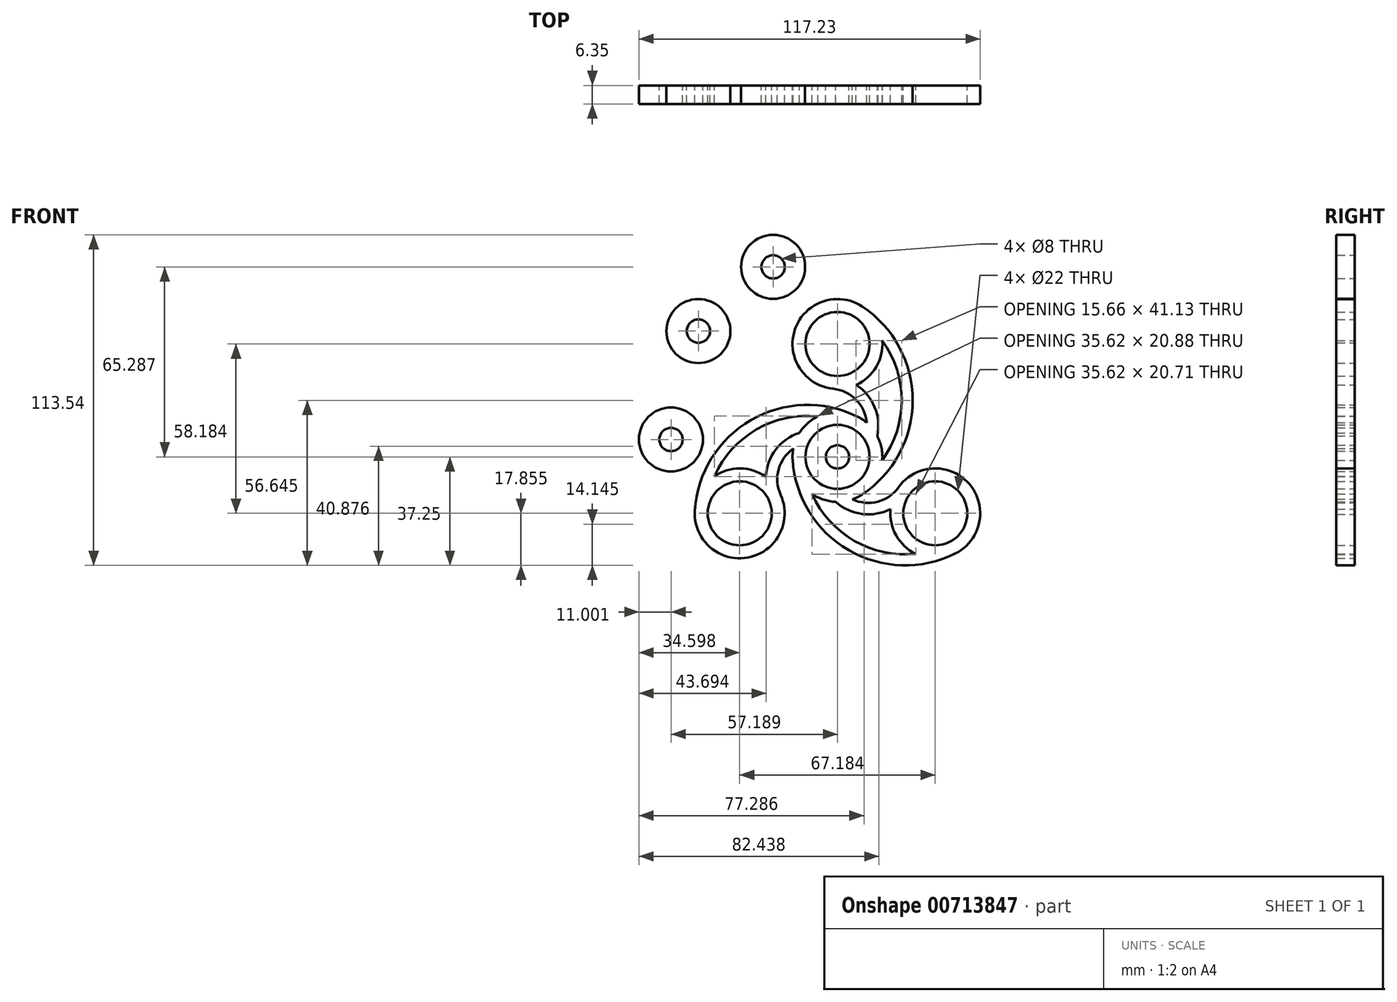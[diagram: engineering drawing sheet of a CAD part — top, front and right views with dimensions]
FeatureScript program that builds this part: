
annotation { "Feature Type Name" : "Feature", "Feature Type Description" : "" }
export const myFeature = defineFeature(function(context is Context, id is Id, definition is map)
    precondition{}
    {
        {
            assignVariable(context, id + "F0", {"name" : "th", "anyValue" : 6.35 * mm});
        }
        {
            var Q0;
            Q0=qCreatedBy(makeId("Front.planeOp"),FACE);
            var sketch = newSketch(context, id + "F1", { "sketchPlane" : qUnion([Q0])});
            skCircle(sketch, "E0", {"center": v(0, 0) * mm, "radius": 11 * mm});
            skLineSegment(sketch, "E1", {"start": v(0, 0) * mm, "end": v(0, 38.79) * mm, "construction": true});
            skArc(sketch, "E2", {"start": v(6.42, 24.74) * mm, "mid": v(13.3, 30.94) * mm, "end": v(15.4, 39.96) * mm});
            skArc(sketch, "E3", {"start": v(10.04, 11.73) * mm, "mid": v(-15.42, 0.92) * mm, "end": v(8.57, -12.85) * mm});
            skArc(sketch, "E4", {"start": v(8.57, -12.85) * mm, "mid": v(25.82, 19.4) * mm, "end": v(8.57, 51.64) * mm});
            skArc(sketch, "E5", {"start": v(10.04, 11.73) * mm, "mid": v(6.42, 19.67) * mm, "end": v(-1.46, 23.41) * mm});
            skCircle(sketch, "E6", {"center": v(0, 38.79) * mm, "radius": 11 * mm});
            skCircle(sketch, "E7", {"center": v(0, 0) * mm, "radius": 4 * mm});
            skArc(sketch, "E8", {"start": v(6.42, 24.74) * mm, "mid": v(12.77, 17.1) * mm, "end": v(13.66, 7.2) * mm});
            skPoint(sketch, "E8.startSnap0", {"position": v(6.42, 19.67) * mm});
            skArc(sketch, "E9", {"start": v(15.4, 39.96) * mm, "mid": v(22.08, 19.4) * mm, "end": v(15.4, -1.17) * mm});
            skArc(sketch, "E10.trimOffspring", {"start": v(8.57, 51.64) * mm, "mid": v(-14.55, 43.96) * mm, "end": v(-1.46, 23.41) * mm});
            skArc(sketch, "E11.trimOffspring", {"start": v(15.4, -1.17) * mm, "mid": v(15.12, 3.14) * mm, "end": v(13.66, 7.2) * mm});
            skCircle(sketch, "E12", {"center": v(0, 38.79) * mm, "radius": 4 * mm});
            skSolve(sketch);
        }
        {
            var Q0;
            Q0 = qSketchRegion(id + "F1", true);
            extrude(context, id + "F2", {"entities" : qUnion([Q0]), "depth" : getVariable(context, 'th'), "offsetDistance" : 25.4 * mm});
        }
        {
            var Q0;
            Q0=makeQuery(id+"F2.opExtrude","SWEPT_BODY",BODY,{"disambiguationData":[OSD([sQuery(id+"F1.wireOp",EDGE,"E0"),sQuery(id+"F1.wireOp",EDGE,"E2"),sQuery(id+"F1.wireOp",EDGE,"E3"),sQuery(id+"F1.wireOp",EDGE,"E4"),sQuery(id+"F1.wireOp",EDGE,"E5"),sQuery(id+"F1.wireOp",EDGE,"E6"),sQuery(id+"F1.wireOp",EDGE,"E8"),sQuery(id+"F1.wireOp",EDGE,"E9"),sQuery(id+"F1.wireOp",EDGE,"E10.trimOffspring"),sQuery(id+"F1.wireOp",EDGE,"E11.trimOffspring")])]});
            var Q1;
            Q1=makeQuery(id+"F2.opExtrude","CAP_EDGE",EDGE,{"disambiguationData":[OSD([sQuery(id+"F1.wireOp",EDGE,"E0")])],"isStart":false});
            circularPattern(context, id + "F3", {"operationType" : NewBodyOperationType.ADD, "entities" : qUnion([Q0]), "axis" : qUnion([Q1]), "angle" : 360 * degree, "instanceCount" : 3, "equalSpace" : true});
        }
        {
            var Q0;
            Q0=makeQuery(id+"F1.imprint","IMPRINT",FACE,{"disambiguationData":[TD([[makeQuery(id+"F1.imprint","IMPRINT",EDGE,{"derivedFrom":sQuery(id+"F1.wireOp",EDGE,"E0")}),1.0]])]});
            extrude(context, id + "F4", {"entities" : qUnion([Q0]), "depth" : getVariable(context, 'th'), "offsetDistance" : 25.4 * mm});
        }
        {
            var Q0;
            Q0=qCreatedBy(makeId("Front.planeOp"),FACE);
            var sketch = newSketch(context, id + "F5", { "sketchPlane" : qUnion([Q0])});
            skCircle(sketch, "E13", {"center": v(-47.79, 43.22) * mm, "radius": 11 * mm});
            skCircle(sketch, "E14", {"center": v(-47.79, 43.22) * mm, "radius": 4 * mm});
            skCircle(sketch, "E15", {"center": v(-57.19, 5.97) * mm, "radius": 11 * mm});
            skCircle(sketch, "E16", {"center": v(-57.19, 5.97) * mm, "radius": 4 * mm});
            skCircle(sketch, "E17", {"center": v(-22.1, 65.29) * mm, "radius": 11 * mm});
            skCircle(sketch, "E18", {"center": v(-22.1, 65.29) * mm, "radius": 4 * mm});
            skSolve(sketch);
        }
        {
            var Q0;
            Q0=makeQuery(id+"F5.imprint","IMPRINT",FACE,{"disambiguationData":[TD([[makeQuery(id+"F5.imprint","IMPRINT",EDGE,{"derivedFrom":sQuery(id+"F5.wireOp",EDGE,"E17")}),1.0]])]});
            extrude(context, id + "F6", {"entities" : qUnion([Q0]), "depth" : getVariable(context, 'th'), "offsetDistance" : 25.4 * mm});
        }
        {
            var Q0;
            Q0=makeQuery(id+"F5.imprint","IMPRINT",FACE,{"disambiguationData":[TD([[makeQuery(id+"F5.imprint","IMPRINT",EDGE,{"derivedFrom":sQuery(id+"F5.wireOp",EDGE,"E13")}),1.0]])]});
            extrude(context, id + "F7", {"entities" : qUnion([Q0]), "depth" : getVariable(context, 'th'), "offsetDistance" : 25.4 * mm});
        }
        {
            var Q0;
            Q0=makeQuery(id+"F5.imprint","IMPRINT",FACE,{"disambiguationData":[TD([[makeQuery(id+"F5.imprint","IMPRINT",EDGE,{"derivedFrom":sQuery(id+"F5.wireOp",EDGE,"E15")}),1.0]])]});
            extrude(context, id + "F8", {"entities" : qUnion([Q0]), "depth" : getVariable(context, 'th'), "offsetDistance" : 25.4 * mm});
        }
    });
